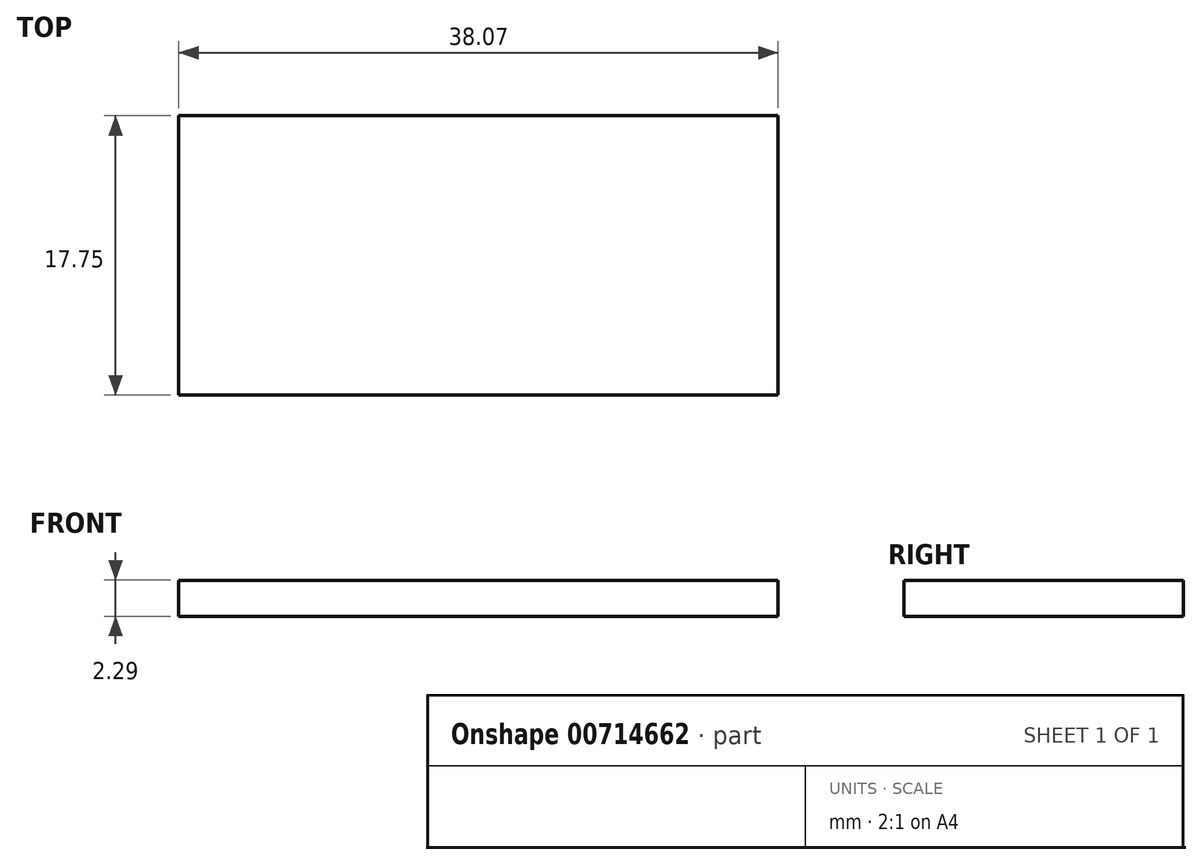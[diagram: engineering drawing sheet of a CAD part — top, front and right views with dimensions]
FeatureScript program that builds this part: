
annotation { "Feature Type Name" : "Feature", "Feature Type Description" : "" }
export const myFeature = defineFeature(function(context is Context, id is Id, definition is map)
    precondition{}
    {
        {
            var Q0;
            Q0=qCreatedBy(makeId("Top.planeOp"),FACE);
            var sketch = newSketch(context, id + "F0", { "sketchPlane" : qUnion([Q0])});
            skLineSegment(sketch, "E0.bottom", {"start": v(2.25, 0) * mm, "end": v(40.32, 0) * mm});
            skLineSegment(sketch, "E0.top", {"start": v(2.25, 17.75) * mm, "end": v(40.32, 17.75) * mm});
            skLineSegment(sketch, "E0.left", {"start": v(2.25, 0) * mm, "end": v(2.25, 17.75) * mm});
            skLineSegment(sketch, "E0.right", {"start": v(40.32, 0) * mm, "end": v(40.32, 17.75) * mm});
            skSolve(sketch);
        }
        {
            var Q0;
            Q0=makeQuery(id+"F0.imprint","IMPRINT",FACE,{"disambiguationData":[TD([[makeQuery(id+"F0.imprint","IMPRINT",EDGE,{"derivedFrom":sQuery(id+"F0.wireOp",EDGE,"E0.bottom")}),1.0]])]});
            extrude(context, id + "F1", {"entities" : qUnion([Q0]), "depth" : 2.3 * mm, "offsetDistance" : 25.4 * mm});
        }
    });
